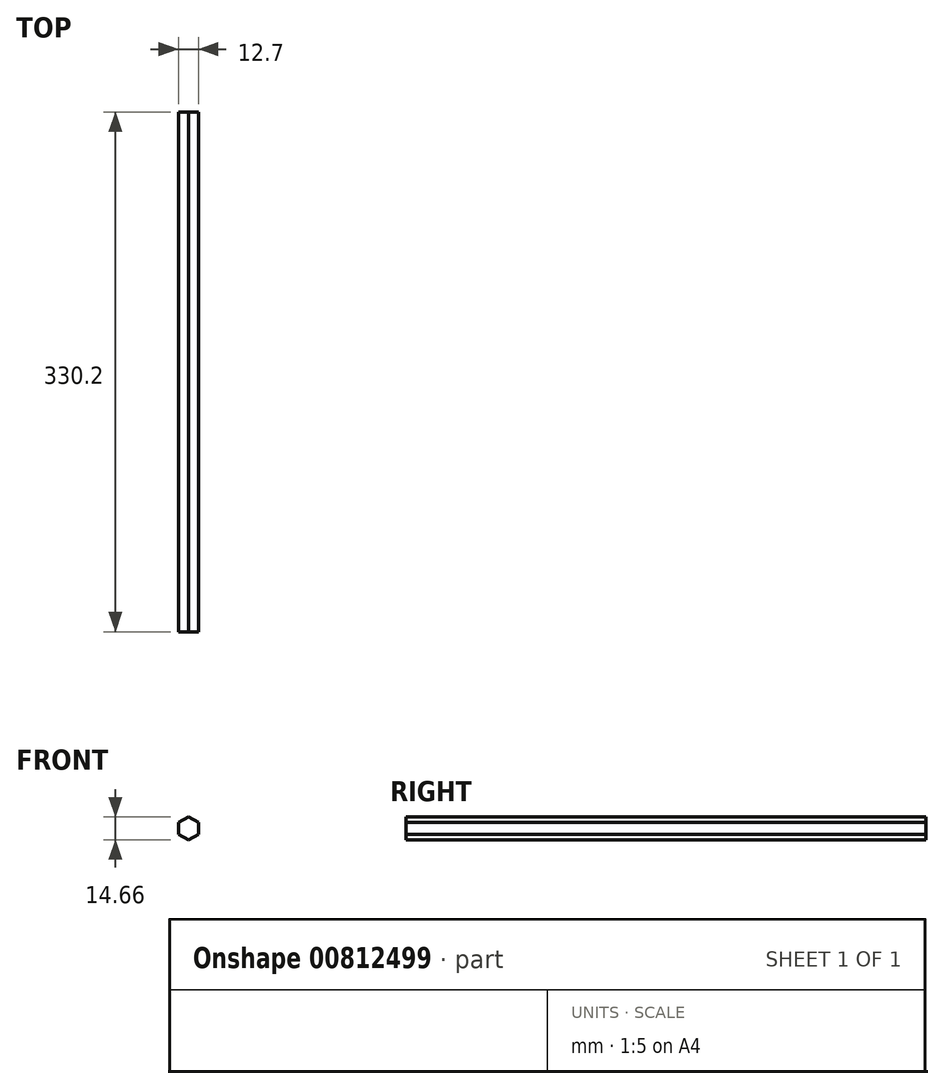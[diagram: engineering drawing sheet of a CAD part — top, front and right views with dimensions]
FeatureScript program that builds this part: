
annotation { "Feature Type Name" : "Feature", "Feature Type Description" : "" }
export const myFeature = defineFeature(function(context is Context, id is Id, definition is map)
    precondition{}
    {
        {
            var Q0;
            Q0=qCreatedBy(makeId("Front.planeOp"),FACE);
            var sketch = newSketch(context, id + "F0", { "sketchPlane" : qUnion([Q0])});
            skCircle(sketch, "E0.cCircle", {"center": v(0, 0) * mm, "radius": 6.35 * mm, "construction": true});
            skLineSegment(sketch, "E0.0", {"start": v(6.35, 3.67) * mm, "end": v(6.35, -3.67) * mm});
            skLineSegment(sketch, "E0.1", {"start": v(6.35, -3.67) * mm, "end": v(0, -7.33) * mm});
            skLineSegment(sketch, "E0.2", {"start": v(0, -7.33) * mm, "end": v(-6.35, -3.67) * mm});
            skLineSegment(sketch, "E0.3", {"start": v(-6.35, -3.67) * mm, "end": v(-6.35, 3.67) * mm});
            skLineSegment(sketch, "E0.4", {"start": v(-6.35, 3.67) * mm, "end": v(0, 7.33) * mm});
            skLineSegment(sketch, "E0.5", {"start": v(0, 7.33) * mm, "end": v(6.35, 3.67) * mm});
            skPoint(sketch, "E0.0.midPoint", {"position": v(6.35, 0) * mm});
            skSolve(sketch);
        }
        {
            var Q0;
            Q0 = qSketchRegion(id + "F0", true);
            extrude(context, id + "F1", {"entities" : qUnion([Q0]), "endBound" : BoundingType.SYMMETRIC, "depth" : 330.2 * mm, "offsetDistance" : 25.4 * mm});
        }
    });
